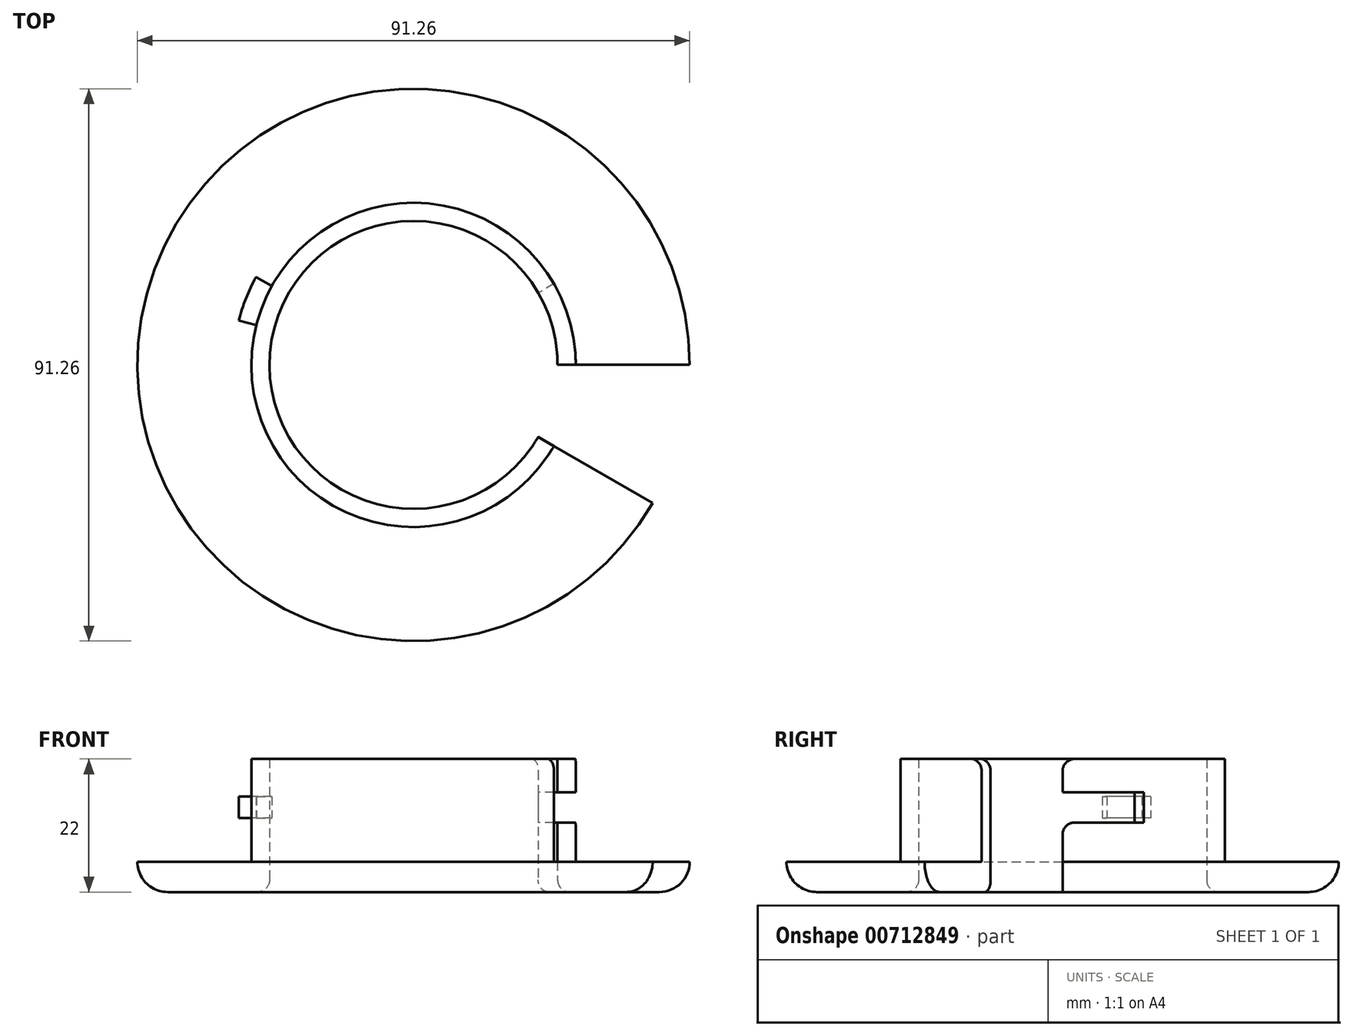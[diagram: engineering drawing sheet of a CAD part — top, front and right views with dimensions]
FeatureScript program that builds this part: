
annotation { "Feature Type Name" : "Feature", "Feature Type Description" : "" }
export const myFeature = defineFeature(function(context is Context, id is Id, definition is map)
    precondition{}
    {
        {
            var Q0;
            Q0=qCreatedBy(makeId("Front.planeOp"),FACE);
            var sketch = newSketch(context, id + "F0", { "sketchPlane" : qUnion([Q0])});
            skLineSegment(sketch, "E0", {"start": v(-26.8, 17) * mm, "end": v(-26.8, 0) * mm});
            skLineSegment(sketch, "E1", {"start": v(-26.8, 0) * mm, "end": v(-45.63, 0) * mm});
            skLineSegment(sketch, "E2", {"start": v(-45.63, 0) * mm, "end": v(-45.63, 0) * mm});
            skLineSegment(sketch, "E3", {"start": v(-40.63, -5) * mm, "end": v(-25.8, -5) * mm});
            skLineSegment(sketch, "E4", {"start": v(-23.8, -3) * mm, "end": v(-23.8, 17) * mm});
            skLineSegment(sketch, "E5", {"start": v(-23.8, 17) * mm, "end": v(-26.8, 17) * mm});
            skPoint(sketch, "E6.visualSharp", {"position": v(-45.63, -5) * mm});
            skPoint(sketch, "E7.visualSharp", {"position": v(-23.8, -5) * mm});
            skArc(sketch, "E7.filletArc", {"start": v(-25.8, -5) * mm, "mid": v(-24.39, -4.41) * mm, "end": v(-23.8, -3) * mm});
            skLineSegment(sketch, "E8", {"start": v(-26.8, 0) * mm, "end": v(0, 0) * mm, "construction": true});
            skLineSegment(sketch, "E9", {"start": v(0, 0) * mm, "end": v(0, 14.6) * mm, "construction": true});
            skPoint(sketch, "E6.filletArc.center.orphan", {"position": v(-40.63, 0) * mm});
            skLineSegment(sketch, "E10", {"start": v(-40.63, -5) * mm, "end": v(-40.63, -5) * mm});
            skArc(sketch, "E11.filletArc", {"start": v(-45.63, 0) * mm, "mid": v(-44.16, -3.54) * mm, "end": v(-40.63, -5) * mm});
            skSolve(sketch);
        }
        {
            var Q0;
            Q0=makeQuery(id+"F0.imprint","IMPRINT",FACE,{"disambiguationData":[TD([[makeQuery(id+"F0.imprint","IMPRINT",EDGE,{"derivedFrom":sQuery(id+"F0.wireOp",EDGE,"E0")}),1.0]])]});
            var Q1;
            Q1=sQuery(id+"F0.wireOp",EDGE,"E9");
            revolve(context, id + "F1", {"surfaceOperationType" : NewSurfaceOperationType.NEW, "entities" : qUnion([Q0]), "axis" : qUnion([Q1]), "revolveType" : RevolveType.FULL});
        }
        {
            var Q0;
            Q0=qCreatedBy(makeId("Top.planeOp"),FACE);
            var sketch = newSketch(context, id + "F2", { "sketchPlane" : qUnion([Q0])});
            skLineSegment(sketch, "E12", {"start": v(0, 0) * mm, "end": v(53.36, 0) * mm});
            skLineSegment(sketch, "E13", {"start": v(0, 0) * mm, "end": v(46.33, -26.75) * mm});
            skLineSegment(sketch, "E14", {"start": v(46.33, -26.75) * mm, "end": v(53.36, 0) * mm});
            skLineSegment(sketch, "E15", {"start": v(0, 0) * mm, "end": v(-39.41, 22.75) * mm, "construction": true});
            skLineSegment(sketch, "E16", {"start": v(0, 0) * mm, "end": v(-45.43, 0) * mm, "construction": true});
            skLineSegment(sketch, "E17", {"start": v(0, 0) * mm, "end": v(-22.81, 39.51) * mm, "construction": true});
            skPoint(sketch, "E18", {"position": v(-26.8, 0) * mm});
            skPoint(sketch, "E19", {"position": v(-23.2, 13.4) * mm});
            skPoint(sketch, "E20", {"position": v(-13.4, 23.2) * mm});
            skSolve(sketch);
        }
        {
            var Q0;
            Q0 = qSketchRegion(id + "F2", true);
            extrude(context, id + "F3", {"entities" : qUnion([Q0]), "operationType" : NewBodyOperationType.REMOVE, "endBound" : BoundingType.THROUGH_ALL, "depth" : 25 * mm, "offsetDistance" : 25 * mm, "hasSecondDirection" : true, "secondDirectionOppositeDirection" : true, "secondDirectionDepth" : 25 * mm});
        }
        {
            var Q0;
            Q0=makeQuery(id+"F1.opRevolve","SWEPT_FACE",FACE,{"disambiguationData":[OSD([sQuery(id+"F0.wireOp",EDGE,"E5")])]});
            cPlane(context, id + "F4", {"entities" : qUnion([Q0]), "cplaneType" : CPlaneType.OFFSET, "offset" : 8 * mm, "oppositeDirection" : true, "width" : 150 * mm, "height" : 150 * mm});
        }
        {
            var Q0;
            Q0=qCreatedBy(id+"F4.planeOp",FACE);
            var sketch = newSketch(context, id + "F5", { "sketchPlane" : qUnion([Q0])});
            skPoint(sketch, "E21", {"position": v(0, 0) * mm});
            skLineSegment(sketch, "E22", {"start": v(0, 0) * mm, "end": v(-32.56, 18.2) * mm, "construction": true});
            skPoint(sketch, "E23", {"position": v(-19.22, 18.68) * mm});
            skLineSegment(sketch, "E24", {"start": v(-26.01, 14.54) * mm, "end": v(-21.98, 12.28) * mm});
            skLineSegment(sketch, "E25", {"start": v(0, 0) * mm, "end": v(30.52, 0) * mm});
            skLineSegment(sketch, "E26", {"start": v(30.52, 0) * mm, "end": v(26.67, 15.4) * mm});
            skLineSegment(sketch, "E27", {"start": v(26.67, 15.4) * mm, "end": v(0, 0) * mm});
            skLineSegment(sketch, "E28.MirrorCS", {"start": v(-21.98, 12.28) * mm, "end": v(-23.09, 5.84) * mm});
            skLineSegment(sketch, "E29.MirrorCS", {"start": v(0, 0) * mm, "end": v(-36.96, 9.35) * mm});
            skArc(sketch, "E30.MirrorCS", {"start": v(-28.9, 7.3) * mm, "mid": v(-27.69, 11.02) * mm, "end": v(-26.01, 14.54) * mm});
            skSolve(sketch);
        }
        {
            var Q0;
            Q0=makeQuery(id+"F5.imprint","IMPRINT",FACE,{"disambiguationData":[TD([[makeQuery(id+"F5.imprint","IMPRINT",EDGE,{"derivedFrom":sQuery(id+"F5.wireOp",EDGE,"E25")}),1.0]])]});
            extrude(context, id + "F6", {"entities" : qUnion([Q0]), "operationType" : NewBodyOperationType.REMOVE, "endBound" : BoundingType.SYMMETRIC, "oppositeDirection" : true, "depth" : 5 * mm, "offsetDistance" : 25 * mm});
        }
        {
            var Q0;
            Q0=makeQuery(id+"F3.boolean.opBoolean","INTERSECT",EDGE,{"derivedFrom":[makeQuery(id+"F1.opRevolve","SWEPT_FACE",FACE,{"disambiguationData":[OSD([sQuery(id+"F0.wireOp",EDGE,"E5")])]}),makeQuery(id+"F3.opExtrude","SWEPT_FACE",FACE,{"disambiguationData":[OSD([sQuery(id+"F2.wireOp",EDGE,"E13")])]})]});
            var Q1;
            Q1=makeQuery(id+"F3.boolean.opBoolean","INTERSECT",EDGE,{"derivedFrom":[makeQuery(id+"F1.opRevolve","SWEPT_FACE",FACE,{"disambiguationData":[OSD([sQuery(id+"F0.wireOp",EDGE,"E5")])]}),makeQuery(id+"F3.opExtrude","SWEPT_FACE",FACE,{"disambiguationData":[OSD([sQuery(id+"F2.wireOp",EDGE,"E12")])]})]});
            var Q2;
            Q2=makeQuery(id+"F6.boolean.opBoolean","COPY",EDGE,{"derivedFrom":makeQuery(id+"F6.opExtrude","CAP_EDGE",EDGE,{"disambiguationData":[OSD([sQuery(id+"F5.wireOp",EDGE,"E25")])],"isStart":true})});
            var Q3;
            Q3=makeQuery(id+"F6.boolean.opBoolean","COPY",EDGE,{"derivedFrom":makeQuery(id+"F6.opExtrude","CAP_EDGE",EDGE,{"disambiguationData":[OSD([sQuery(id+"F5.wireOp",EDGE,"E25")])],"isStart":false})});
            fillet(context, id + "F7", {"entities" : qUnion([Q0, Q1, Q2, Q3]), "radius" : 2 * mm, "tangentPropagation" : true, "allowEdgeOverflow" : false});
        }
        {
            var Q0;
            Q0=makeQuery(id+"F5.imprint","IMPRINT",FACE,{"disambiguationData":[TD([[makeQuery(id+"F5.imprint","IMPRINT",EDGE,{"derivedFrom":sQuery(id+"F5.wireOp",EDGE,"E24")}),-1.0]])]});
            extrude(context, id + "F8", {"entities" : qUnion([Q0]), "operationType" : NewBodyOperationType.ADD, "endBound" : BoundingType.SYMMETRIC, "depth" : 3.6 * mm, "offsetDistance" : 25 * mm});
        }
    });
